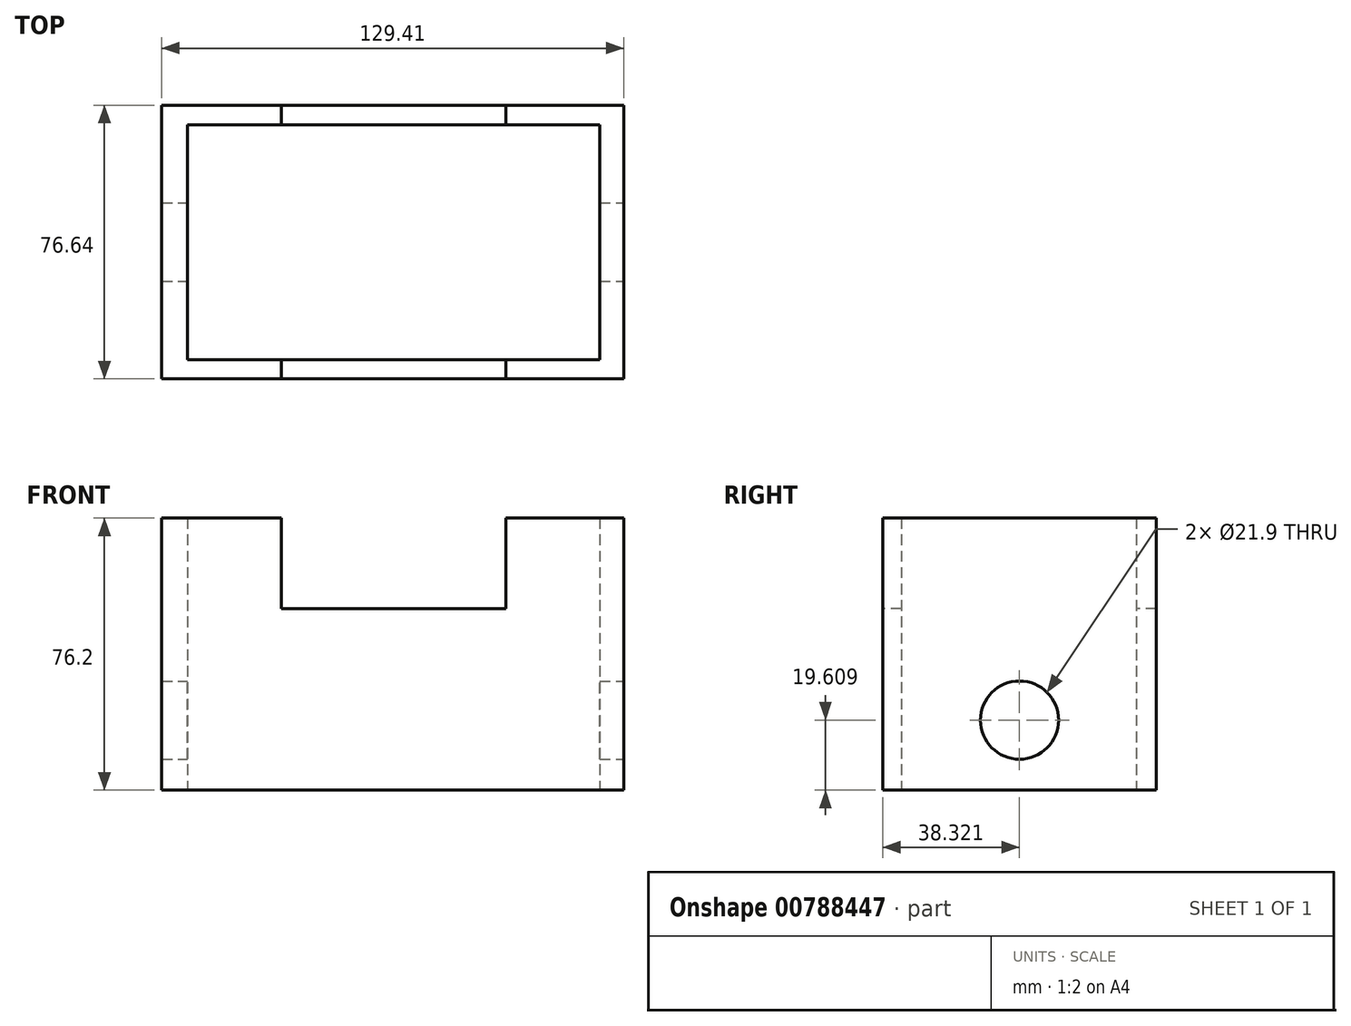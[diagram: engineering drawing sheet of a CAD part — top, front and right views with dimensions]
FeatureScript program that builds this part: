
annotation { "Feature Type Name" : "Feature", "Feature Type Description" : "" }
export const myFeature = defineFeature(function(context is Context, id is Id, definition is map)
    precondition{}
    {
        {
            var Q0;
            Q0=qCreatedBy(makeId("Top.planeOp"),FACE);
            var sketch = newSketch(context, id + "F0", { "sketchPlane" : qUnion([Q0])});
            skLineSegment(sketch, "E0.bottom", {"start": v(-59.16, 31.2) * mm, "end": v(70.25, 31.2) * mm});
            skLineSegment(sketch, "E0.top", {"start": v(-59.16, -45.43) * mm, "end": v(70.25, -45.43) * mm});
            skLineSegment(sketch, "E0.left", {"start": v(-59.16, 31.2) * mm, "end": v(-59.16, -45.43) * mm});
            skLineSegment(sketch, "E0.right", {"start": v(70.25, 31.2) * mm, "end": v(70.25, -45.43) * mm});
            skLineSegment(sketch, "E1.bottom", {"start": v(-51.93, 25.67) * mm, "end": v(63.5, 25.67) * mm});
            skLineSegment(sketch, "E1.top", {"start": v(-51.93, -40.13) * mm, "end": v(63.5, -40.13) * mm});
            skLineSegment(sketch, "E1.left", {"start": v(-51.93, 25.67) * mm, "end": v(-51.93, -40.13) * mm});
            skLineSegment(sketch, "E1.right", {"start": v(63.5, 25.67) * mm, "end": v(63.5, -40.13) * mm});
            skSolve(sketch);
        }
        {
            var Q0;
            Q0=makeQuery(id+"F0.imprint","IMPRINT",FACE,{"disambiguationData":[TD([[makeQuery(id+"F0.imprint","IMPRINT",EDGE,{"derivedFrom":sQuery(id+"F0.wireOp",EDGE,"E0.bottom")}),-1.0]])]});
            extrude(context, id + "F1", {"entities" : qUnion([Q0]), "depth" : 50.8 * mm, "offsetDistance" : 25.4 * mm});
        }
        {
            var Q0;
            Q0=makeQuery(id+"F1.opExtrude","CAP_FACE",FACE,{"disambiguationData":[OSD([sQuery(id+"F0.wireOp",EDGE,"E0.bottom"),sQuery(id+"F0.wireOp",EDGE,"E0.top"),sQuery(id+"F0.wireOp",EDGE,"E0.left"),sQuery(id+"F0.wireOp",EDGE,"E0.right"),sQuery(id+"F0.wireOp",EDGE,"E1.bottom"),sQuery(id+"F0.wireOp",EDGE,"E1.top"),sQuery(id+"F0.wireOp",EDGE,"E1.left"),sQuery(id+"F0.wireOp",EDGE,"E1.right")])],"isStart":false});
            var sketch = newSketch(context, id + "F2", { "sketchPlane" : qUnion([Q0])});
            skLineSegment(sketch, "E2", {"start": v(-25.67, 31.2) * mm, "end": v(-25.67, 25.67) * mm});
            skLineSegment(sketch, "E3", {"start": v(-25.67, -40.13) * mm, "end": v(-25.67, -45.43) * mm});
            skLineSegment(sketch, "E4", {"start": v(37.23, 31.2) * mm, "end": v(37.23, 25.67) * mm});
            skLineSegment(sketch, "E5", {"start": v(37.23, -40.13) * mm, "end": v(37.23, -45.43) * mm});
            skSolve(sketch);
        }
        {
            var Q0;
            {var subQ4=sQuery(id+"F2.wireOp",EDGE,"E2");Q0=makeQuery(id+"F2.imprint","IMPRINT",FACE,{"disambiguationData":[TD([[makeQuery(id+"F2.imprint","IMPRINT",EDGE,{"derivedFrom":subQ4}),-1.0]])]});}
            var Q1;
            {var subQ4=sQuery(id+"F2.wireOp",EDGE,"E4");Q1=makeQuery(id+"F2.imprint","IMPRINT",FACE,{"disambiguationData":[TD([[makeQuery(id+"F2.imprint","IMPRINT",EDGE,{"derivedFrom":subQ4}),1.0]])]});}
            extrude(context, id + "F3", {"entities" : qUnion([Q0, Q1]), "operationType" : NewBodyOperationType.ADD, "depth" : 25.4 * mm, "offsetDistance" : 25.4 * mm});
        }
        {
            var Q0;
            {var subQ0=sQuery(id+"F0.wireOp",EDGE,"E0.right");Q0=makeQuery(id+"F3.boolean.opBoolean","MERGE",FACE,{"derivedFrom":[makeQuery(id+"F1.opExtrude","SWEPT_FACE",FACE,{"disambiguationData":[OSD([subQ0])]}),makeQuery(id+"F3.opExtrude","SWEPT_FACE",FACE,{"disambiguationData":[OSD([subQ0])]})]});}
            var sketch = newSketch(context, id + "F4", { "sketchPlane" : qUnion([Q0])});
            skCircle(sketch, "E6", {"center": v(-7.1, 19.6) * mm, "radius": 10.95 * mm});
            skPoint(sketch, "E6.centerSnap0", {"position": v(-7.1, 76.2) * mm});
            skSolve(sketch);
        }
        {
            var Q0;
            Q0=makeQuery(id+"F4.imprint","IMPRINT",FACE,{"disambiguationData":[TD([[makeQuery(id+"F4.imprint","IMPRINT",EDGE,{"derivedFrom":sQuery(id+"F4.wireOp",EDGE,"E6")}),1.0]])]});
            extrude(context, id + "F5", {"entities" : qUnion([Q0]), "operationType" : NewBodyOperationType.REMOVE, "oppositeDirection" : true, "depth" : 190.25 * mm, "offsetDistance" : 25.4 * mm});
        }
    });
